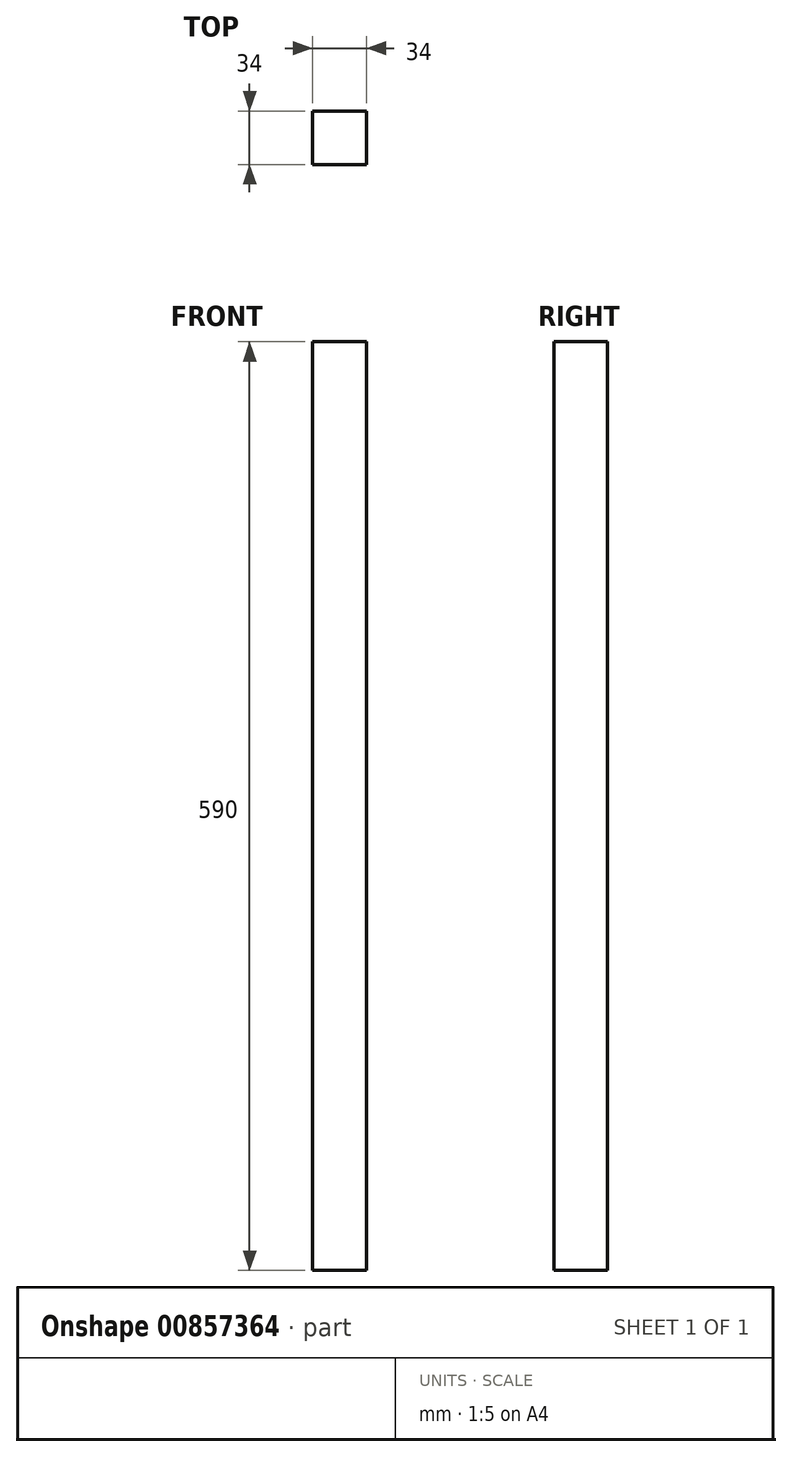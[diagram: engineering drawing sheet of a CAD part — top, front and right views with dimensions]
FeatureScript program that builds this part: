
annotation { "Feature Type Name" : "Feature", "Feature Type Description" : "" }
export const myFeature = defineFeature(function(context is Context, id is Id, definition is map)
    precondition{}
    {
        {
            var Q0;
            Q0=qCreatedBy(makeId("Top.planeOp"),FACE);
            var sketch = newSketch(context, id + "F0", { "sketchPlane" : qUnion([Q0])});
            skLineSegment(sketch, "E0.bottom", {"start": v(0, 0) * mm, "end": v(-34, 0) * mm});
            skLineSegment(sketch, "E0.top", {"start": v(0, -34) * mm, "end": v(-34, -34) * mm});
            skLineSegment(sketch, "E0.left", {"start": v(0, 0) * mm, "end": v(0, -34) * mm});
            skLineSegment(sketch, "E0.right", {"start": v(-34, 0) * mm, "end": v(-34, -34) * mm});
            skSolve(sketch);
        }
        {
            var Q0;
            Q0=makeQuery(id+"F0.imprint","IMPRINT",FACE,{"disambiguationData":[TD([[makeQuery(id+"F0.imprint","IMPRINT",EDGE,{"derivedFrom":sQuery(id+"F0.wireOp",EDGE,"E0.bottom")}),1.0]])]});
            extrude(context, id + "F1", {"entities" : qUnion([Q0]), "oppositeDirection" : true, "depth" : 590 * mm, "offsetDistance" : 25 * mm});
        }
    });
